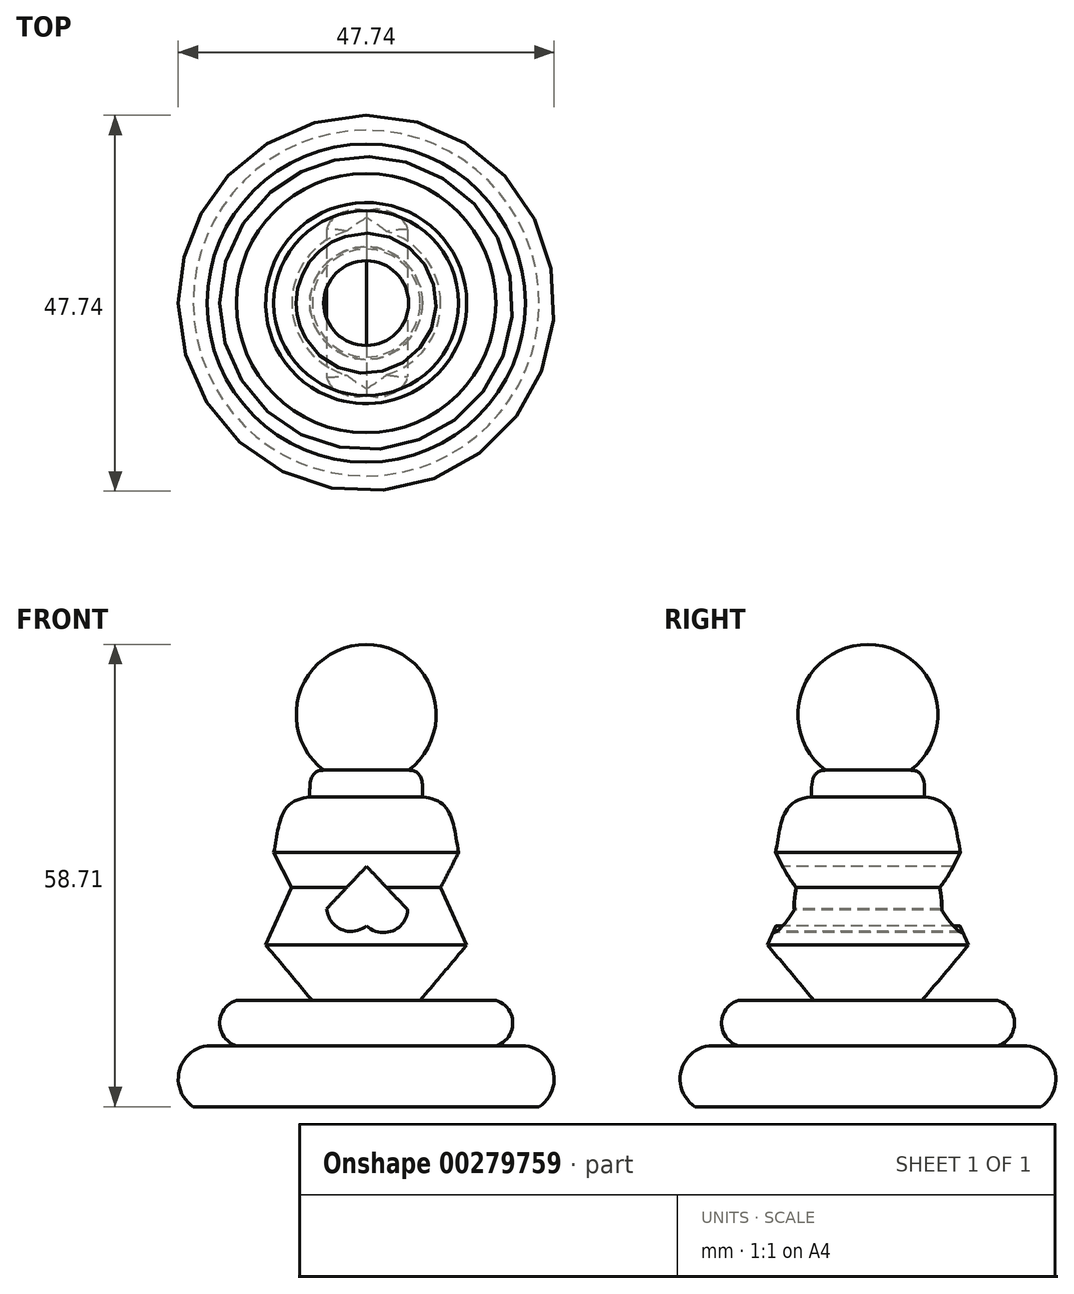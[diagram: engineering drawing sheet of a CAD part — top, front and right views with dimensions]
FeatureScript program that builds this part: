
annotation { "Feature Type Name" : "Feature", "Feature Type Description" : "" }
export const myFeature = defineFeature(function(context is Context, id is Id, definition is map)
    precondition{}
    {
        {
            var Q0;
            Q0=qCreatedBy(makeId("Front.planeOp"),FACE);
            var sketch = newSketch(context, id + "F0", { "sketchPlane" : qUnion([Q0])});
            skFitSpline(sketch, "E0", {"points": [v(1.42, 10) * mm, v(9.7, 9.18) * mm, v(11.74, 3.04) * mm, v(12.77, -8.72) * mm, v(7.4, -29.45) * mm], "startDerivative": vector(47.97, 3.57) * mm, "endDerivative": vector(5.74, -42.96) * mm});
            skLineSegment(sketch, "E1", {"start": v(0, 30.92) * mm, "end": v(0, -39.2) * mm});
            skLineSegment(sketch, "E2", {"start": v(1.42, 10) * mm, "end": v(0, 10) * mm});
            skArc(sketch, "E3", {"start": v(5.4, 13.5) * mm, "mid": v(-2.84, 29) * mm, "end": v(0, 11.69) * mm});
            skLineSegment(sketch, "E4", {"start": v(5.4, 13.5) * mm, "end": v(0, 13.5) * mm});
            skLineSegment(sketch, "E5", {"start": v(11.74, 3.04) * mm, "end": v(9.45, -1.4) * mm});
            skLineSegment(sketch, "E6", {"start": v(9.45, -1.4) * mm, "end": v(12.77, -8.72) * mm});
            skFitSpline(sketch, "E7", {"points": [v(6.84, -15.75) * mm, v(12.77, -8.72) * mm], "startDerivative": vector(8.9, 10.4) * mm, "endDerivative": vector(8.9, 10.4) * mm});
            skFitSpline(sketch, "E8", {"points": [v(5.4, 13.5) * mm, v(6.08, 13.4) * mm, v(6.7, 12.94) * mm, v(7.08, 12.06) * mm, v(7.17, 11.11) * mm, v(7.17, 10.11) * mm], "startDerivative": vector(4, -0.2) * mm, "endDerivative": vector(-0.14, -5.16) * mm});
            skLineSegment(sketch, "E9", {"start": v(6.84, -15.75) * mm, "end": v(0, -15.75) * mm});
            skSolve(sketch);
        }
        {
            var Q0;
            {var subQ1=sQuery(id+"F0.wireOp",EDGE,"E0");Q0=makeQuery(id+"F0.imprint","IMPRINT",FACE,{"disambiguationData":[TD([[makeQuery(id+"F0.imprint","IMPRINT",EDGE,{"derivedFrom":subQ1}),-1.0]])]});}
            var Q1;
            {var subQ0=sQuery(id+"F0.wireOp",EDGE,"los3iYxt-0uX2-z3dp-LnZg-N1HU59Y3sD1d");var subQ1=makeQuery(id+"F0.imprint","INTERSECT",VERTEX,{"derivedFrom":[subQ0,sQuery(id+"F0.wireOp",EDGE,"E0")]});Q1=makeQuery(id+"F0.imprint","IMPRINT",FACE,{"disambiguationData":[TD([[makeQuery(id+"F0.imprint","IMPRINT",EDGE,{"disambiguationData":[TD([[subQ1,1.0]])],"derivedFrom":subQ0}),1.0]])]});}
            var Q2;
            {var subQ0=sQuery(id+"F0.wireOp",EDGE,"E2");Q2=makeQuery(id+"F0.imprint","IMPRINT",FACE,{"disambiguationData":[TD([[makeQuery(id+"F0.imprint","IMPRINT",EDGE,{"derivedFrom":subQ0}),-1.0]])]});}
            var Q3;
            {var subQ0=sQuery(id+"F0.wireOp",EDGE,"V3LdIwS1-vv7Z-afae-8zuc-7Wr7gSZbDaTL");var subQ1=sQuery(id+"F0.wireOp",EDGE,"E1");var subQ2=makeQuery(id+"F0.imprint","INTERSECT",VERTEX,{"derivedFrom":[subQ1,subQ0]});Q3=makeQuery(id+"F0.imprint","IMPRINT",FACE,{"disambiguationData":[TD([[makeQuery(id+"F0.imprint","IMPRINT",EDGE,{"disambiguationData":[TD([[subQ2,1.0]])],"derivedFrom":subQ1}),1.0]])]});}
            var Q4;
            {var subQ0=sQuery(id+"F0.wireOp",EDGE,"E4");Q4=makeQuery(id+"F0.imprint","IMPRINT",FACE,{"disambiguationData":[TD([[makeQuery(id+"F0.imprint","IMPRINT",EDGE,{"derivedFrom":subQ0}),-1.0]])]});}
            var Q5;
            {var subQ0=sQuery(id+"F0.wireOp",EDGE,"ca8068d0-8d46-4f08-a441-d71eff8d5d09");Q5=makeQuery(id+"F0.imprint","IMPRINT",FACE,{"disambiguationData":[TD([[makeQuery(id+"F0.imprint","IMPRINT",EDGE,{"derivedFrom":subQ0}),1.0]])]});}
            var Q6;
            Q6=sQuery(id+"F0.wireOp",EDGE,"E1");
            revolve(context, id + "F1", {"entities" : qUnion([Q0, Q1, Q2, Q3, Q4, Q5]), "axis" : qUnion([Q6]), "revolveType" : RevolveType.FULL});
        }
        {
            var Q0;
            Q0=qCreatedBy(makeId("Front.planeOp"),FACE);
            var sketch = newSketch(context, id + "F2", { "sketchPlane" : qUnion([Q0])});
            skArc(sketch, "E10", {"start": v(0.05, -6.26) * mm, "mid": v(3.3, -6.92) * mm, "end": v(5.28, -4.25) * mm});
            skArc(sketch, "E11", {"start": v(-5.02, -4.1) * mm, "mid": v(-3.15, -6.73) * mm, "end": v(0.05, -6.26) * mm});
            skLineSegment(sketch, "E12", {"start": v(5.28, -4.25) * mm, "end": v(0.05, 1.3) * mm});
            skLineSegment(sketch, "E13", {"start": v(0.05, 1.3) * mm, "end": v(-5.02, -4.1) * mm});
            skSolve(sketch);
        }
        {
            var Q0;
            Q0 = qSketchRegion(id + "F2", true);
            extrude(context, id + "F3", {"entities" : qUnion([Q0]), "operationType" : NewBodyOperationType.REMOVE, "endBound" : BoundingType.SYMMETRIC, "oppositeDirection" : true, "depth" : 63.5 * mm});
        }
        {
            var Q0;
            Q0=qCreatedBy(makeId("Front.planeOp"),FACE);
            var sketch = newSketch(context, id + "F4", { "sketchPlane" : qUnion([Q0])});
            skLineSegment(sketch, "E14", {"start": v(0, -29.24) * mm, "end": v(20.21, -29.24) * mm});
            skLineSegment(sketch, "E15", {"start": v(16.47, -15.75) * mm, "end": v(11.63, -15.75) * mm});
            skLineSegment(sketch, "E16", {"start": v(16.47, -21.5) * mm, "end": v(20.21, -21.5) * mm});
            skArc(sketch, "E17", {"start": v(16.47, -21.5) * mm, "mid": v(18.62, -18.62) * mm, "end": v(16.47, -15.75) * mm});
            skLineSegment(sketch, "E18", {"start": v(20.21, -29.24) * mm, "end": v(21.97, -29.24) * mm});
            skArc(sketch, "E19", {"start": v(21.97, -29.24) * mm, "mid": v(23.77, -24.76) * mm, "end": v(20.21, -21.5) * mm});
            skLineSegment(sketch, "E20", {"start": v(11.63, -15.75) * mm, "end": v(0, -15.75) * mm});
            skLineSegment(sketch, "E21", {"start": v(0, -41.58) * mm, "end": v(0, -11.23) * mm});
            skSolve(sketch);
        }
        {
            var Q0;
            {var subQ0=sQuery(id+"F4.wireOp",EDGE,"E14");Q0=makeQuery(id+"F4.imprint","IMPRINT",FACE,{"disambiguationData":[TD([[makeQuery(id+"F4.imprint","IMPRINT",EDGE,{"derivedFrom":subQ0}),1.0]])]});}
            var Q1;
            Q1=sQuery(id+"F4.wireOp",EDGE,"E21");
            revolve(context, id + "F5", {"entities" : qUnion([Q0]), "axis" : qUnion([Q1]), "revolveType" : RevolveType.FULL});
        }
    });
